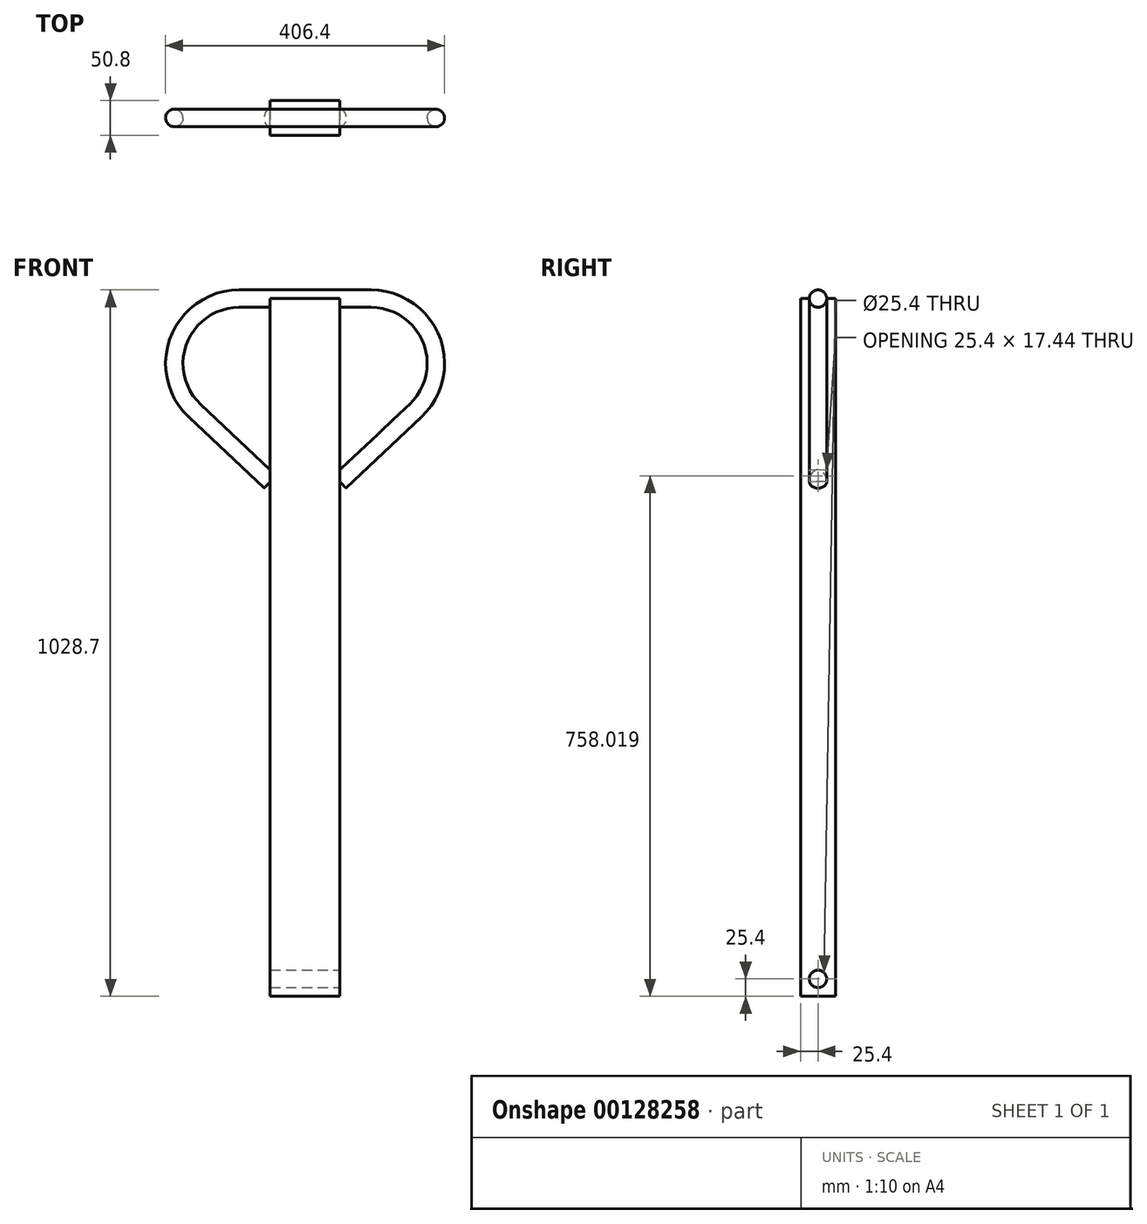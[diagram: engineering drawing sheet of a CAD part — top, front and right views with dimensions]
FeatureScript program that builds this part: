
annotation { "Feature Type Name" : "Feature", "Feature Type Description" : "" }
export const myFeature = defineFeature(function(context is Context, id is Id, definition is map)
    precondition{}
    {
        {
            var Q0;
            Q0=qCreatedBy(makeId("Front.planeOp"),FACE);
            var sketch = newSketch(context, id + "F0", { "sketchPlane" : qUnion([Q0])});
            skLineSegment(sketch, "E0.bottom", {"start": v(50.8, 508) * mm, "end": v(-50.8, 508) * mm});
            skLineSegment(sketch, "E0.top", {"start": v(50.8, -508) * mm, "end": v(-50.8, -508) * mm});
            skLineSegment(sketch, "E0.left", {"start": v(50.8, 508) * mm, "end": v(50.8, -508) * mm});
            skLineSegment(sketch, "E0.right", {"start": v(-50.8, 508) * mm, "end": v(-50.8, -508) * mm});
            skPoint(sketch, "E0.middle", {"position": v(0, 0) * mm});
            skSolve(sketch);
        }
        {
            var Q0;
            Q0 = qSketchRegion(id + "F0", true);
            extrude(context, id + "F1", {"entities" : qUnion([Q0]), "endBound" : BoundingType.SYMMETRIC, "depth" : 50.8 * mm});
        }
        {
            var Q0;
            Q0=qCreatedBy(makeId("Front.planeOp"),FACE);
            var sketch = newSketch(context, id + "F2", { "sketchPlane" : qUnion([Q0])});
            skLineSegment(sketch, "E1", {"start": v(0, 0) * mm, "end": v(0, 508) * mm, "construction": true});
            skLineSegment(sketch, "E2", {"start": v(0, 508) * mm, "end": v(96.07, 508) * mm});
            skLineSegment(sketch, "E3", {"start": v(50.8, 241.3) * mm, "end": v(160.78, 344.8) * mm});
            skArc(sketch, "E4", {"start": v(160.78, 344.8) * mm, "mid": v(183.85, 448.38) * mm, "end": v(96.07, 508) * mm});
            skLineSegment(sketch, "E5.MirrorCS", {"start": v(0, 508) * mm, "end": v(-96.07, 508) * mm});
            skLineSegment(sketch, "E6.MirrorCS", {"start": v(-50.8, 241.3) * mm, "end": v(-160.78, 344.8) * mm});
            skArc(sketch, "E7.MirrorCS", {"start": v(-160.78, 344.8) * mm, "mid": v(-183.85, 448.38) * mm, "end": v(-96.07, 508) * mm});
            skSolve(sketch);
        }
        {
            var Q0;
            Q0=qCreatedBy(makeId("Right.planeOp"),FACE);
            var sketch = newSketch(context, id + "F3", { "sketchPlane" : qUnion([Q0])});
            skCircle(sketch, "E8", {"center": v(0, 508) * mm, "radius": 12.7 * mm});
            skSolve(sketch);
        }
        {
            var Q0;
            Q0 = qSketchRegion(id + "F3", true);
            var Q1;
            Q1=sQuery(id+"F2.wireOp",EDGE,"E2");
            var Q2;
            Q2=sQuery(id+"F2.wireOp",EDGE,"E4");
            var Q3;
            Q3=sQuery(id+"F2.wireOp",EDGE,"E3");
            sweep(context, id + "F4", {"operationType" : NewBodyOperationType.ADD, "profiles" : qUnion([Q0]), "path" : qUnion([Q1, Q2, Q3])});
        }
        {
            var Q0;
            Q0 = qSketchRegion(id + "F3", true);
            var Q1;
            Q1=sQuery(id+"F2.wireOp",EDGE,"E5.MirrorCS");
            var Q2;
            Q2=sQuery(id+"F2.wireOp",EDGE,"E7.MirrorCS");
            var Q3;
            Q3=sQuery(id+"F2.wireOp",EDGE,"E6.MirrorCS");
            sweep(context, id + "F5", {"operationType" : NewBodyOperationType.ADD, "profiles" : qUnion([Q0]), "path" : qUnion([Q1, Q2, Q3])});
        }
        {
            var Q0;
            Q0=makeQuery(id+"F1.opExtrude","SWEPT_FACE",FACE,{"disambiguationData":[OSD([sQuery(id+"F0.wireOp",EDGE,"E0.left")])]});
            var sketch = newSketch(context, id + "F6", { "sketchPlane" : qUnion([Q0])});
            skLineSegment(sketch, "E9", {"start": v(0, -508) * mm, "end": v(0, -482.6) * mm, "construction": true});
            skPoint(sketch, "E9.endSnap0", {"position": v(0, -508) * mm});
            skLineSegment(sketch, "E10", {"start": v(0, -482.6) * mm, "end": v(25.4, -482.6) * mm, "construction": true});
            skCircle(sketch, "E11", {"center": v(0, -482.6) * mm, "radius": 12.7 * mm});
            skSolve(sketch);
        }
        {
            var Q0;
            Q0 = qSketchRegion(id + "F6", true);
            extrude(context, id + "F7", {"entities" : qUnion([Q0]), "operationType" : NewBodyOperationType.REMOVE, "endBound" : BoundingType.THROUGH_ALL, "oppositeDirection" : true, "depth" : 25.4 * mm});
        }
    });
